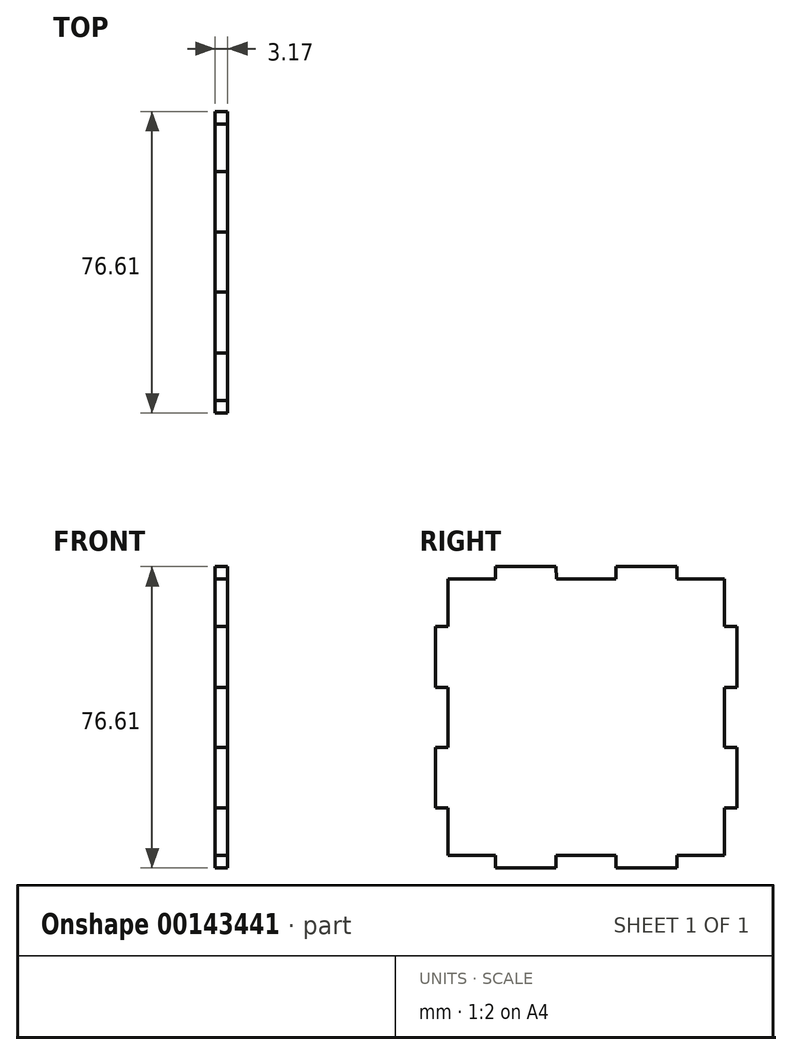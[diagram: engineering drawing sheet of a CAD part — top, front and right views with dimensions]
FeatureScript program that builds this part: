
annotation { "Feature Type Name" : "Feature", "Feature Type Description" : "" }
export const myFeature = defineFeature(function(context is Context, id is Id, definition is map)
    precondition{}
    {
        {
            var Q0;
            Q0=qCreatedBy(makeId("Right.planeOp"),FACE);
            var sketch = newSketch(context, id + "F0", { "sketchPlane" : qUnion([Q0])});
            skLineSegment(sketch, "E0.bottom", {"start": v(-29.03, 52.39) * mm, "end": v(-16.97, 52.39) * mm});
            skLineSegment(sketch, "E0.top", {"start": v(-29.03, -17.87) * mm, "end": v(-16.97, -17.87) * mm});
            skLineSegment(sketch, "E0.left", {"start": v(-29.03, 52.39) * mm, "end": v(-29.03, 40.32) * mm});
            skLineSegment(sketch, "E0.right", {"start": v(41.22, 52.39) * mm, "end": v(41.22, 40.32) * mm});
            skLineSegment(sketch, "E1.0", {"start": v(-16.97, 55.56) * mm, "end": v(-1.52, 55.56) * mm});
            skLineSegment(sketch, "E1.1", {"start": v(-32.2, 40.32) * mm, "end": v(-32.2, 24.88) * mm});
            skLineSegment(sketch, "E1.2", {"start": v(-16.97, -21.05) * mm, "end": v(-1.52, -21.05) * mm});
            skLineSegment(sketch, "E1.3", {"start": v(44.4, 40.32) * mm, "end": v(44.4, 24.88) * mm});
            skLineSegment(sketch, "E2", {"start": v(-29.03, 40.32) * mm, "end": v(-32.2, 40.32) * mm});
            skLineSegment(sketch, "E3", {"start": v(-29.03, 24.88) * mm, "end": v(-32.2, 24.88) * mm});
            skLineSegment(sketch, "E4", {"start": v(-29.03, 9.64) * mm, "end": v(-32.2, 9.64) * mm});
            skLineSegment(sketch, "E5", {"start": v(-29.03, -5.8) * mm, "end": v(-32.2, -5.8) * mm});
            skLineSegment(sketch, "E6", {"start": v(41.22, 40.32) * mm, "end": v(44.4, 40.32) * mm});
            skLineSegment(sketch, "E7", {"start": v(41.22, 24.88) * mm, "end": v(44.4, 24.88) * mm});
            skLineSegment(sketch, "E8", {"start": v(41.22, 9.64) * mm, "end": v(44.4, 9.64) * mm});
            skLineSegment(sketch, "E9", {"start": v(41.22, -5.8) * mm, "end": v(44.4, -5.8) * mm});
            skLineSegment(sketch, "E10.trimOffspring", {"start": v(-32.2, 9.64) * mm, "end": v(-32.2, -5.8) * mm});
            skLineSegment(sketch, "E11.trimOffspring", {"start": v(-29.03, -5.8) * mm, "end": v(-29.03, -17.87) * mm});
            skLineSegment(sketch, "E12.trimOffspring", {"start": v(-29.03, 24.88) * mm, "end": v(-29.03, 9.64) * mm});
            skLineSegment(sketch, "E13.trimOffspring", {"start": v(41.22, 24.88) * mm, "end": v(41.22, 9.64) * mm});
            skLineSegment(sketch, "E14.trimOffspring", {"start": v(44.4, 9.64) * mm, "end": v(44.4, -5.8) * mm});
            skLineSegment(sketch, "E15.trimOffspring", {"start": v(41.22, -5.8) * mm, "end": v(41.22, -17.87) * mm});
            skLineSegment(sketch, "E16", {"start": v(-16.97, 52.39) * mm, "end": v(-16.97, 55.56) * mm});
            skLineSegment(sketch, "E17", {"start": v(-1.47, 52.39) * mm, "end": v(-1.52, 55.56) * mm});
            skLineSegment(sketch, "E18", {"start": v(13.72, 52.39) * mm, "end": v(13.72, 55.56) * mm});
            skLineSegment(sketch, "E19", {"start": v(29.16, 52.39) * mm, "end": v(29.16, 55.56) * mm});
            skLineSegment(sketch, "E20", {"start": v(-16.97, -17.87) * mm, "end": v(-16.97, -21.05) * mm});
            skLineSegment(sketch, "E21", {"start": v(-1.52, -17.87) * mm, "end": v(-1.52, -21.05) * mm});
            skLineSegment(sketch, "E22", {"start": v(13.72, -17.87) * mm, "end": v(13.72, -21.05) * mm});
            skLineSegment(sketch, "E23", {"start": v(29.16, -17.87) * mm, "end": v(29.16, -21.05) * mm});
            skLineSegment(sketch, "E24.trimOffspring", {"start": v(-1.52, -17.87) * mm, "end": v(13.72, -17.87) * mm});
            skLineSegment(sketch, "E25.trimOffspring", {"start": v(13.72, -21.05) * mm, "end": v(29.16, -21.05) * mm});
            skLineSegment(sketch, "E26.trimOffspring", {"start": v(29.16, -17.87) * mm, "end": v(41.22, -17.87) * mm});
            skLineSegment(sketch, "E27.trimOffspring", {"start": v(29.16, 52.39) * mm, "end": v(41.22, 52.39) * mm});
            skLineSegment(sketch, "E28.trimOffspring", {"start": v(-1.47, 52.39) * mm, "end": v(13.72, 52.39) * mm});
            skLineSegment(sketch, "E29.trimOffspring", {"start": v(13.72, 55.56) * mm, "end": v(29.16, 55.56) * mm});
            skSolve(sketch);
        }
        {
            var Q0;
            Q0=makeQuery(id+"F0.imprint","IMPRINT",FACE,{"disambiguationData":[TD([[makeQuery(id+"F0.imprint","IMPRINT",EDGE,{"derivedFrom":sQuery(id+"F0.wireOp",EDGE,"E0.bottom")}),-1.0]])]});
            extrude(context, id + "F1", {"entities" : qUnion([Q0]), "depth" : 3.17 * mm});
        }
    });
